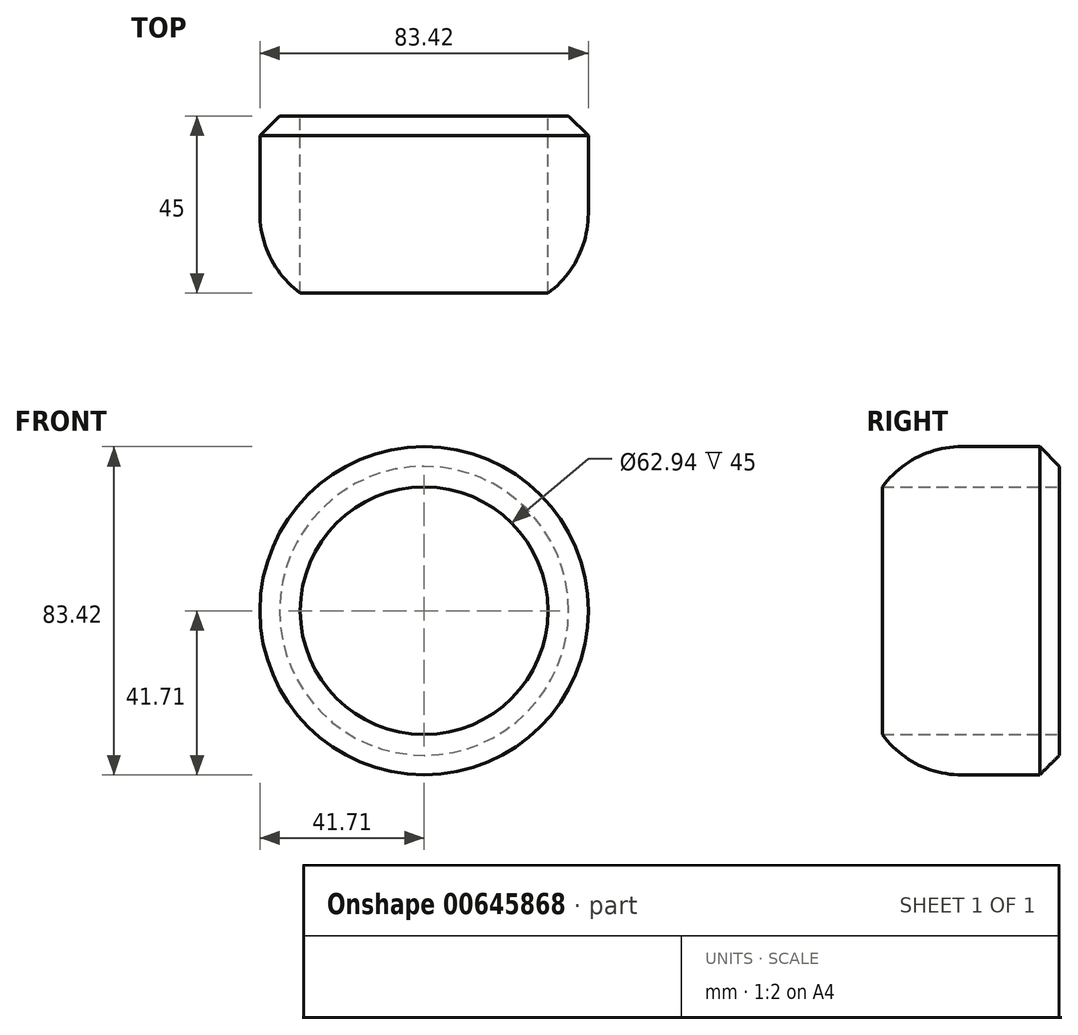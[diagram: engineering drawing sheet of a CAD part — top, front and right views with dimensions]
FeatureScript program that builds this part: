
annotation { "Feature Type Name" : "Feature", "Feature Type Description" : "" }
export const myFeature = defineFeature(function(context is Context, id is Id, definition is map)
    precondition{}
    {
        {
            var Q0;
            Q0=qCreatedBy(makeId("Front.planeOp"),FACE);
            var sketch = newSketch(context, id + "F0", { "sketchPlane" : qUnion([Q0])});
            skCircle(sketch, "E0", {"center": v(0, 0) * mm, "radius": 41.7 * mm});
            skCircle(sketch, "E1", {"center": v(0, 0) * mm, "radius": 31.47 * mm});
            skCircle(sketch, "E2", {"center": v(0, 0) * mm, "radius": 6 * mm});
            skSolve(sketch);
        }
        {
            var Q0;
            Q0=makeQuery(id+"F0.imprint","IMPRINT",FACE,{"disambiguationData":[TD([[makeQuery(id+"F0.imprint","IMPRINT",EDGE,{"derivedFrom":sQuery(id+"F0.wireOp",EDGE,"E0")}),1.0]])]});
            extrude(context, id + "F1", {"entities" : qUnion([Q0]), "depth" : 45 * mm, "offsetDistance" : 25 * mm});
        }
        {
            var Q0;
            Q0=makeQuery(id+"F1.opExtrude","CAP_EDGE",EDGE,{"disambiguationData":[OSD([sQuery(id+"F0.wireOp",EDGE,"E0")])],"isStart":false});
            fillet(context, id + "F2", {"entities" : qUnion([Q0]), "radius" : 25.1 * mm, "tangentPropagation" : true, "allowEdgeOverflow" : false});
        }
        {
            var Q0;
            Q0=makeQuery(id+"F1.opExtrude","CAP_EDGE",EDGE,{"disambiguationData":[OSD([sQuery(id+"F0.wireOp",EDGE,"E0")])],"isStart":true});
            chamfer(context, id + "F3", {"entities" : qUnion([Q0]), "width" : 5 * mm, "tangentPropagation" : true});
        }
    });
